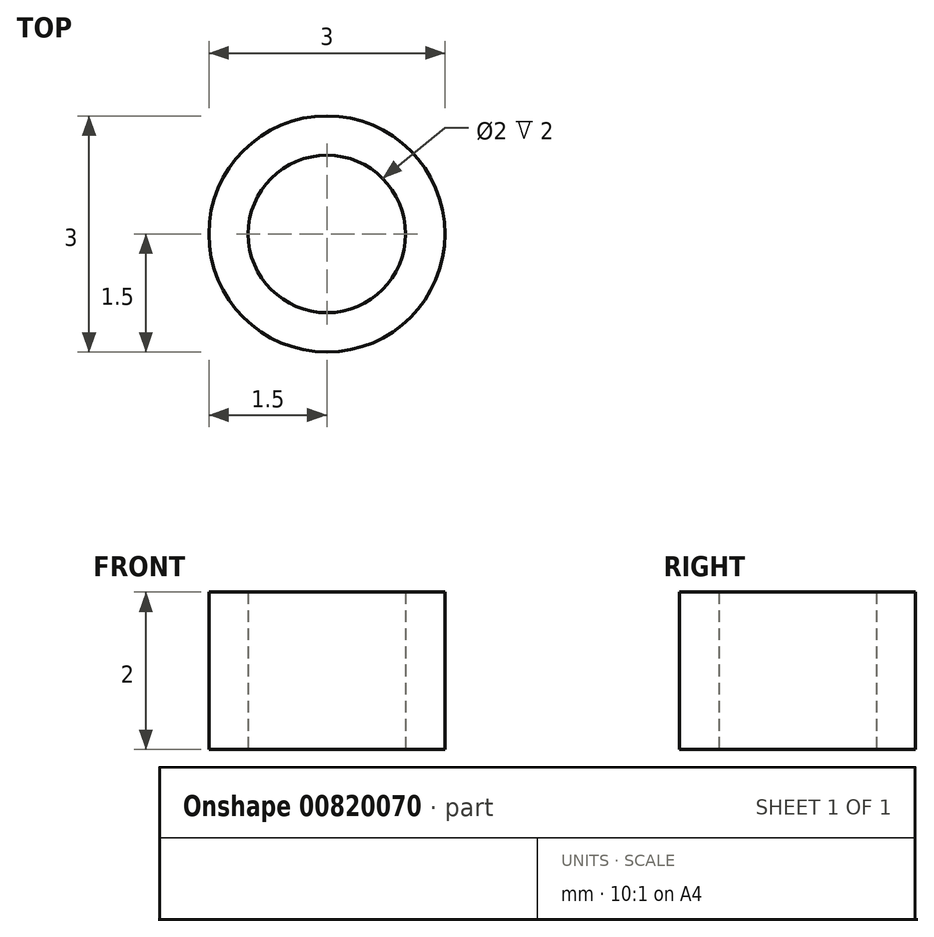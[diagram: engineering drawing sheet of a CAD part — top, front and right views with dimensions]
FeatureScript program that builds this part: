
annotation { "Feature Type Name" : "Feature", "Feature Type Description" : "" }
export const myFeature = defineFeature(function(context is Context, id is Id, definition is map)
    precondition{}
    {
        {
            var Q0;
            Q0=qCreatedBy(makeId("Top.planeOp"),FACE);
            var sketch = newSketch(context, id + "F0", { "sketchPlane" : qUnion([Q0])});
            skCircle(sketch, "E0", {"center": v(0, 0) * mm, "radius": 1.5 * mm});
            skCircle(sketch, "E1", {"center": v(0, 0) * mm, "radius": 1 * mm});
            skSolve(sketch);
        }
        {
            var Q0;
            Q0=makeQuery(id+"F0.imprint","IMPRINT",FACE,{"disambiguationData":[TD([[makeQuery(id+"F0.imprint","IMPRINT",EDGE,{"derivedFrom":sQuery(id+"F0.wireOp",EDGE,"E0")}),1.0]])]});
            extrude(context, id + "F1", {"entities" : qUnion([Q0]), "depth" : 2 * mm, "offsetDistance" : 25 * mm});
        }
    });
